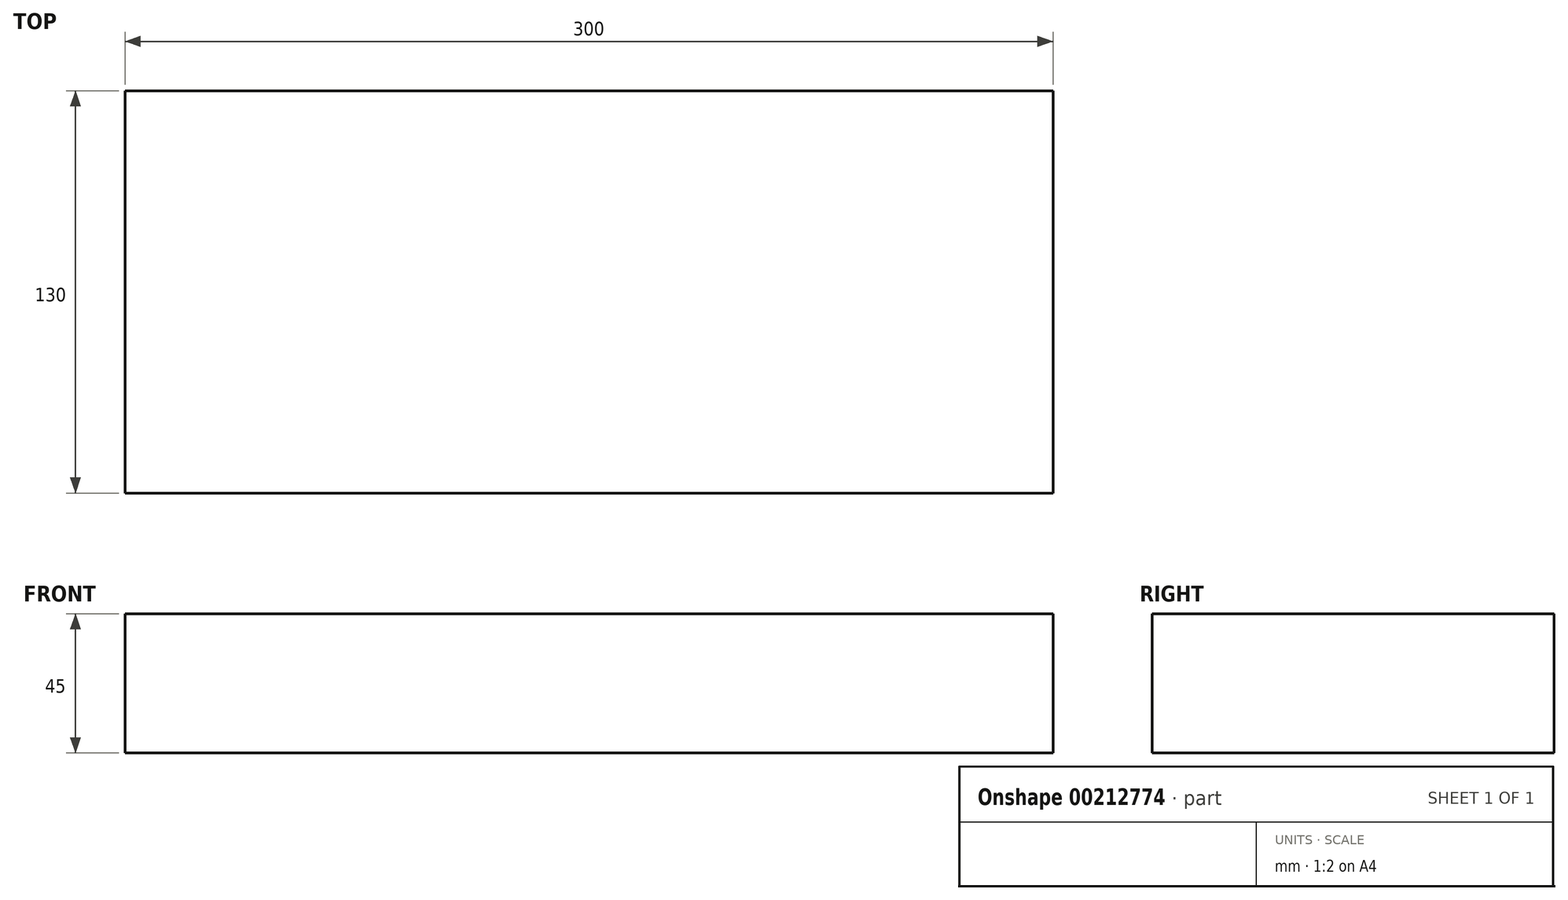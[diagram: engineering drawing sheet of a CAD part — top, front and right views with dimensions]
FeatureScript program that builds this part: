
annotation { "Feature Type Name" : "Feature", "Feature Type Description" : "" }
export const myFeature = defineFeature(function(context is Context, id is Id, definition is map)
    precondition{}
    {
        {
            var Q0;
            Q0=qCreatedBy(makeId("Top.planeOp"),FACE);
            var sketch = newSketch(context, id + "F0", { "sketchPlane" : qUnion([Q0])});
            skLineSegment(sketch, "E0.bottom", {"start": v(-126.82, 68.36) * mm, "end": v(173.18, 68.36) * mm});
            skLineSegment(sketch, "E0.top", {"start": v(-126.82, -61.64) * mm, "end": v(173.18, -61.64) * mm});
            skLineSegment(sketch, "E0.left", {"start": v(-126.82, 68.36) * mm, "end": v(-126.82, -61.64) * mm});
            skLineSegment(sketch, "E0.right", {"start": v(173.18, 68.36) * mm, "end": v(173.18, -61.64) * mm});
            skSolve(sketch);
        }
        {
            var Q0;
            Q0=makeQuery(id+"F0.imprint","IMPRINT",FACE,{"disambiguationData":[TD([[makeQuery(id+"F0.imprint","IMPRINT",EDGE,{"derivedFrom":sQuery(id+"F0.wireOp",EDGE,"E0.bottom")}),-1.0]])]});
            extrude(context, id + "F1", {"entities" : qUnion([Q0]), "depth" : 45 * mm});
        }
    });
